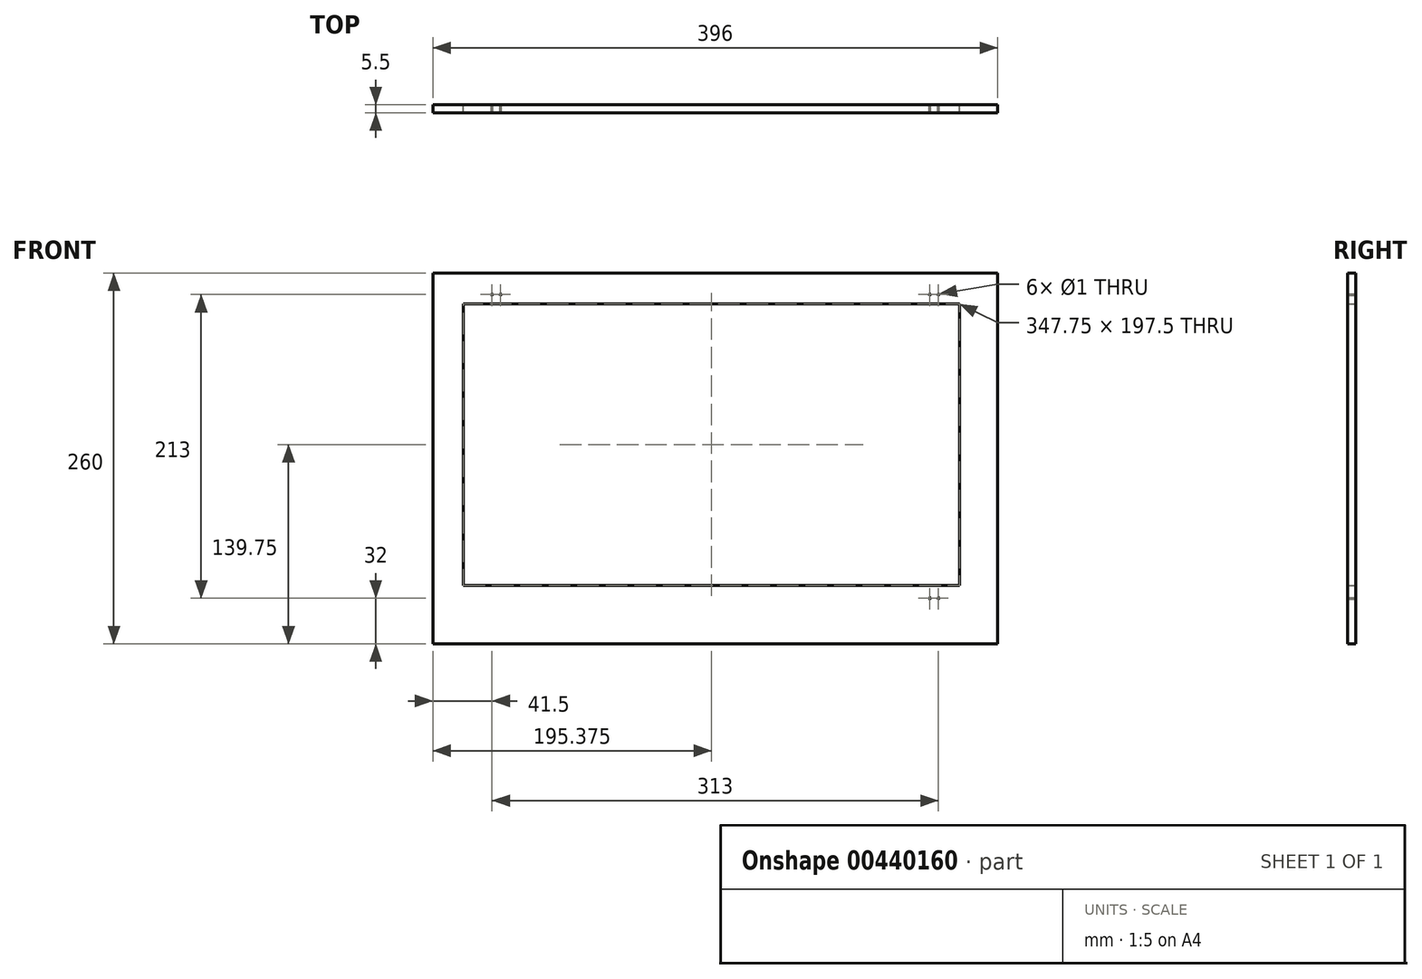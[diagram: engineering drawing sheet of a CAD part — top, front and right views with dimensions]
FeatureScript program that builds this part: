
annotation { "Feature Type Name" : "Feature", "Feature Type Description" : "" }
export const myFeature = defineFeature(function(context is Context, id is Id, definition is map)
    precondition{}
    {
        {
            var Q0;
            Q0=qCreatedBy(makeId("Front.planeOp"),FACE);
            var sketch = newSketch(context, id + "F0", { "sketchPlane" : qUnion([Q0])});
            skLineSegment(sketch, "E0.bottom", {"start": v(-198, 130) * mm, "end": v(198, 130) * mm});
            skLineSegment(sketch, "E0.top", {"start": v(-198, -130) * mm, "end": v(198, -130) * mm});
            skLineSegment(sketch, "E0.left", {"start": v(-198, 130) * mm, "end": v(-198, -130) * mm});
            skLineSegment(sketch, "E0.right", {"start": v(198, 130) * mm, "end": v(198, -130) * mm});
            skPoint(sketch, "E1", {"position": v(0, 130) * mm});
            skPoint(sketch, "E2", {"position": v(-198, 0) * mm});
            skLineSegment(sketch, "E3.bottom", {"start": v(-176.5, 108.5) * mm, "end": v(171.25, 108.5) * mm});
            skLineSegment(sketch, "E3.top", {"start": v(-176.5, -89) * mm, "end": v(171.25, -89) * mm});
            skLineSegment(sketch, "E3.left", {"start": v(-176.5, 108.5) * mm, "end": v(-176.5, -89) * mm});
            skLineSegment(sketch, "E3.right", {"start": v(171.25, 108.5) * mm, "end": v(171.25, -89) * mm});
            skPoint(sketch, "E4", {"position": v(-156.5, 115) * mm});
            skPoint(sketch, "E5", {"position": v(-150.5, 115) * mm});
            skCircle(sketch, "E6", {"center": v(-156.5, 115) * mm, "radius": 0.5 * mm});
            skCircle(sketch, "E7", {"center": v(-150.5, 115) * mm, "radius": 0.5 * mm});
            skPoint(sketch, "E8", {"position": v(156.5, 115) * mm});
            skPoint(sketch, "E9", {"position": v(150.5, 115) * mm});
            skCircle(sketch, "E10", {"center": v(150.5, 115) * mm, "radius": 0.5 * mm});
            skCircle(sketch, "E11", {"center": v(156.5, 115) * mm, "radius": 0.5 * mm});
            skPoint(sketch, "E12", {"position": v(156.5, -98) * mm});
            skPoint(sketch, "E13", {"position": v(150.5, -98) * mm});
            skCircle(sketch, "E14", {"center": v(150.5, -98) * mm, "radius": 0.5 * mm});
            skCircle(sketch, "E15", {"center": v(156.5, -98) * mm, "radius": 0.5 * mm});
            skSolve(sketch);
        }
        {
            var Q0;
            Q0 = qSketchRegion(id + "F0", true);
            extrude(context, id + "F1", {"entities" : qUnion([Q0]), "depth" : 5.5 * mm});
        }
    });
